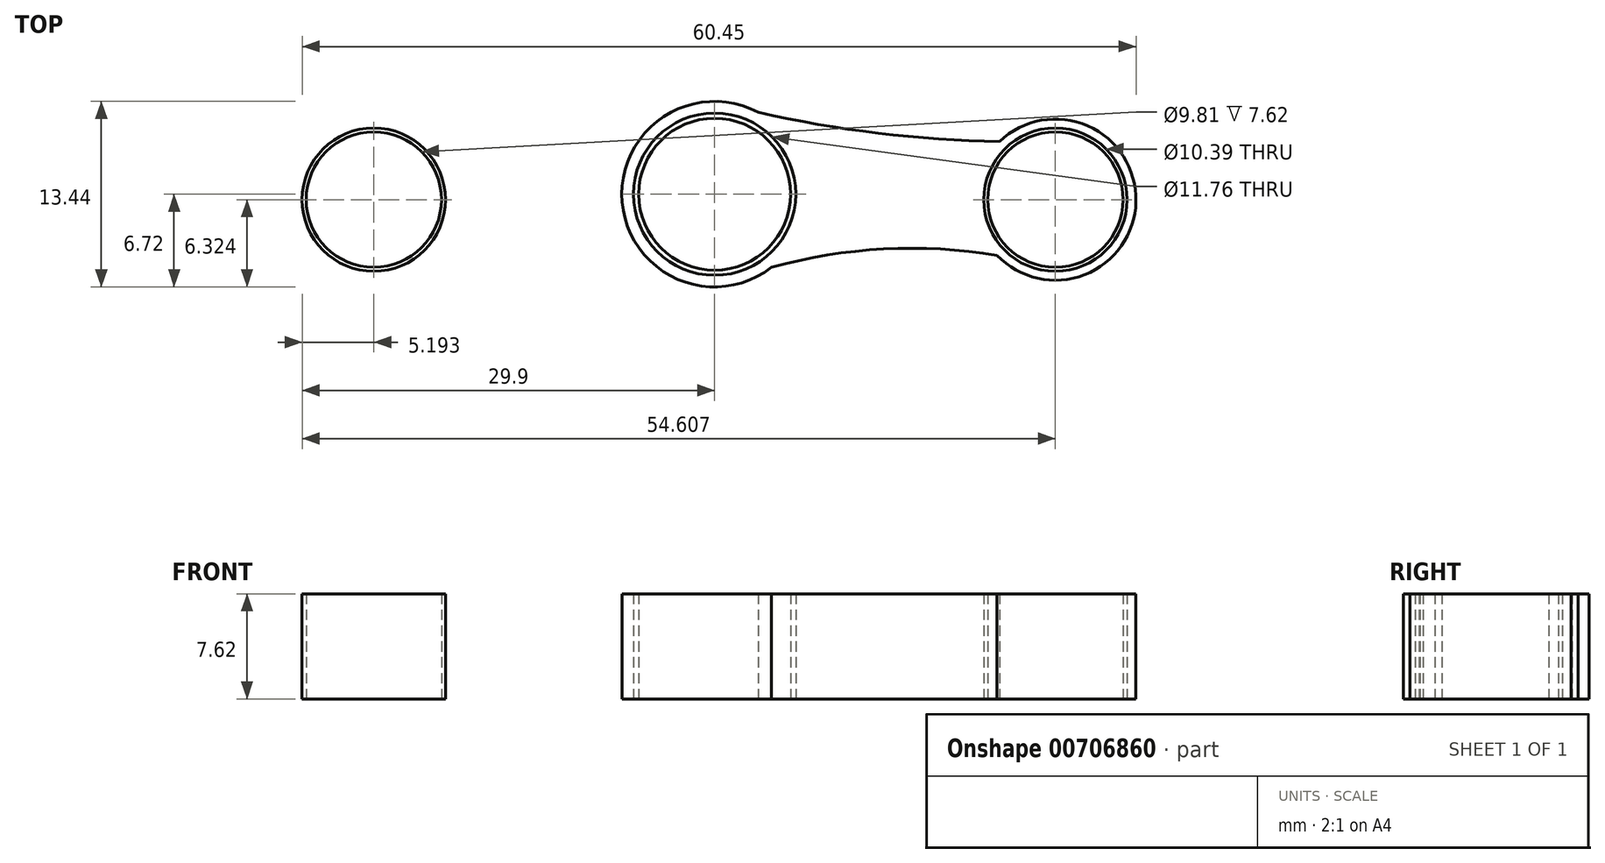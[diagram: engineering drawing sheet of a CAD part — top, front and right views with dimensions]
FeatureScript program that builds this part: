
annotation { "Feature Type Name" : "Feature", "Feature Type Description" : "" }
export const myFeature = defineFeature(function(context is Context, id is Id, definition is map)
    precondition{}
    {
        {
            var Q0;
            Q0=qCreatedBy(makeId("Top.planeOp"),FACE);
            var sketch = newSketch(context, id + "F0", { "sketchPlane" : qUnion([Q0])});
            skCircle(sketch, "E0", {"center": v(0, 0) * mm, "radius": 6.72 * mm});
            skArc(sketch, "E1", {"start": v(0, 6.72) * mm, "mid": v(10.24, 4.63) * mm, "end": v(20.66, 3.82) * mm});
            skArc(sketch, "E2", {"start": v(20.48, -4.43) * mm, "mid": v(10.08, -4.15) * mm, "end": v(0, -6.72) * mm});
            skArc(sketch, "E3", {"start": v(20.48, -4.43) * mm, "mid": v(30.55, -0.53) * mm, "end": v(20.66, 3.82) * mm});
            skArc(sketch, "E4.MirrorCS", {"start": v(-20.48, -4.43) * mm, "mid": v(-10.08, -4.15) * mm, "end": v(0, -6.72) * mm});
            skArc(sketch, "E5.MirrorCS", {"start": v(0, 6.72) * mm, "mid": v(-10.24, 4.63) * mm, "end": v(-20.66, 3.82) * mm});
            skArc(sketch, "E6.MirrorCS", {"start": v(-20.48, -4.43) * mm, "mid": v(-30.55, -0.53) * mm, "end": v(-20.66, 3.82) * mm});
            skCircle(sketch, "E7", {"center": v(0, 0) * mm, "radius": 5.88 * mm});
            skCircle(sketch, "E8", {"center": v(0, 0) * mm, "radius": 5.5 * mm});
            skCircle(sketch, "E9", {"center": v(24.7, -0.4) * mm, "radius": 5.2 * mm});
            skCircle(sketch, "E10", {"center": v(24.7, -0.4) * mm, "radius": 4.9 * mm});
            skCircle(sketch, "E11.MirrorC", {"center": v(-24.7, -0.4) * mm, "radius": 4.9 * mm});
            skCircle(sketch, "E12.MirrorC", {"center": v(-24.7, -0.4) * mm, "radius": 5.2 * mm});
            skSolve(sketch);
        }
        {
            var Q0;
            {var subQ0=sQuery(id+"F0.wireOp",EDGE,"E1");var subQ1=sQuery(id+"F0.wireOp",EDGE,"E0");var subQ3=makeQuery(id+"F0.imprint","INTERSECT",VERTEX,{"derivedFrom":[subQ1,subQ0]});Q0=makeQuery(id+"F0.imprint","IMPRINT",FACE,{"disambiguationData":[TD([[makeQuery(id+"F0.imprint","IMPRINT",EDGE,{"disambiguationData":[TD([[subQ3,-1.0]])],"derivedFrom":subQ1}),1.0]])]});}
            var Q1;
            {var subQ0=sQuery(id+"F0.wireOp",EDGE,"E5.MirrorCS");var subQ1=sQuery(id+"F0.wireOp",EDGE,"E0");var subQ3=makeQuery(id+"F0.imprint","INTERSECT",VERTEX,{"derivedFrom":[subQ1,subQ0]});Q1=makeQuery(id+"F0.imprint","IMPRINT",FACE,{"disambiguationData":[TD([[makeQuery(id+"F0.imprint","IMPRINT",EDGE,{"disambiguationData":[TD([[subQ3,1.0]])],"derivedFrom":subQ1}),1.0]])]});}
            var Q2;
            {var subQ0=sQuery(id+"F0.wireOp",EDGE,"E4.MirrorCS");var subQ1=sQuery(id+"F0.wireOp",EDGE,"E0");var subQ3=makeQuery(id+"F0.imprint","INTERSECT",VERTEX,{"derivedFrom":[subQ1,subQ0]});Q2=makeQuery(id+"F0.imprint","IMPRINT",FACE,{"disambiguationData":[TD([[makeQuery(id+"F0.imprint","IMPRINT",EDGE,{"disambiguationData":[TD([[subQ3,-1.0]])],"derivedFrom":subQ1}),1.0]])]});}
            var Q3;
            {var subQ0=sQuery(id+"F0.wireOp",EDGE,"E2");var subQ1=sQuery(id+"F0.wireOp",EDGE,"E0");var subQ3=makeQuery(id+"F0.imprint","INTERSECT",VERTEX,{"derivedFrom":[subQ1,subQ0]});Q3=makeQuery(id+"F0.imprint","IMPRINT",FACE,{"disambiguationData":[TD([[makeQuery(id+"F0.imprint","IMPRINT",EDGE,{"disambiguationData":[TD([[subQ3,1.0]])],"derivedFrom":subQ1}),1.0]])]});}
            var Q4;
            {var subQ0=sQuery(id+"F0.wireOp",EDGE,"E6.MirrorCS");Q4=makeQuery(id+"F0.imprint","IMPRINT",FACE,{"disambiguationData":[TD([[makeQuery(id+"F0.imprint","IMPRINT",EDGE,{"derivedFrom":subQ0}),-1.0]])]});}
            var Q5;
            {var subQ0=sQuery(id+"F0.wireOp",EDGE,"E3");Q5=makeQuery(id+"F0.imprint","IMPRINT",FACE,{"disambiguationData":[TD([[makeQuery(id+"F0.imprint","IMPRINT",EDGE,{"derivedFrom":subQ0}),1.0]])]});}
            var Q6;
            Q6=makeQuery(id+"F0.imprint","IMPRINT",FACE,{"disambiguationData":[TD([[makeQuery(id+"F0.imprint","IMPRINT",EDGE,{"derivedFrom":sQuery(id+"F0.wireOp",EDGE,"5411be69-d2da-4510-bf12-6406d50423480.MirrorC")}),-1.0]])]});
            var Q7;
            Q7=makeQuery(id+"F0.imprint","IMPRINT",FACE,{"disambiguationData":[TD([[makeQuery(id+"F0.imprint","IMPRINT",EDGE,{"derivedFrom":sQuery(id+"F0.wireOp",EDGE,"STYxCkdz-04jQ-iMR0-E1Cy-XjOkfdsy9LAS")}),1.0]])]});
            var Q8;
            Q8=makeQuery(id+"F0.imprint","IMPRINT",FACE,{"disambiguationData":[TD([[makeQuery(id+"F0.imprint","IMPRINT",EDGE,{"derivedFrom":sQuery(id+"F0.wireOp",EDGE,"E8")}),1.0]])]});
            var Q9;
            Q9=makeQuery(id+"F0.imprint","IMPRINT",FACE,{"disambiguationData":[TD([[makeQuery(id+"F0.imprint","IMPRINT",EDGE,{"derivedFrom":sQuery(id+"F0.wireOp",EDGE,"E7")}),-1.0]])]});
            var Q10;
            Q10=makeQuery(id+"F0.imprint","IMPRINT",FACE,{"disambiguationData":[TD([[makeQuery(id+"F0.imprint","IMPRINT",EDGE,{"derivedFrom":sQuery(id+"F0.wireOp",EDGE,"E10")}),1.0]])]});
            var Q11;
            Q11=makeQuery(id+"F0.imprint","IMPRINT",FACE,{"disambiguationData":[TD([[makeQuery(id+"F0.imprint","IMPRINT",EDGE,{"derivedFrom":sQuery(id+"F0.wireOp",EDGE,"E11.MirrorC")}),-1.0]])]});
            extrude(context, id + "F1", {"entities" : qUnion([Q0, Q1, Q2, Q3, Q4, Q5, Q6, Q7, Q8, Q9, Q10, Q11]), "depth" : 7.62 * mm, "offsetDistance" : 25.4 * mm});
        }
    });
